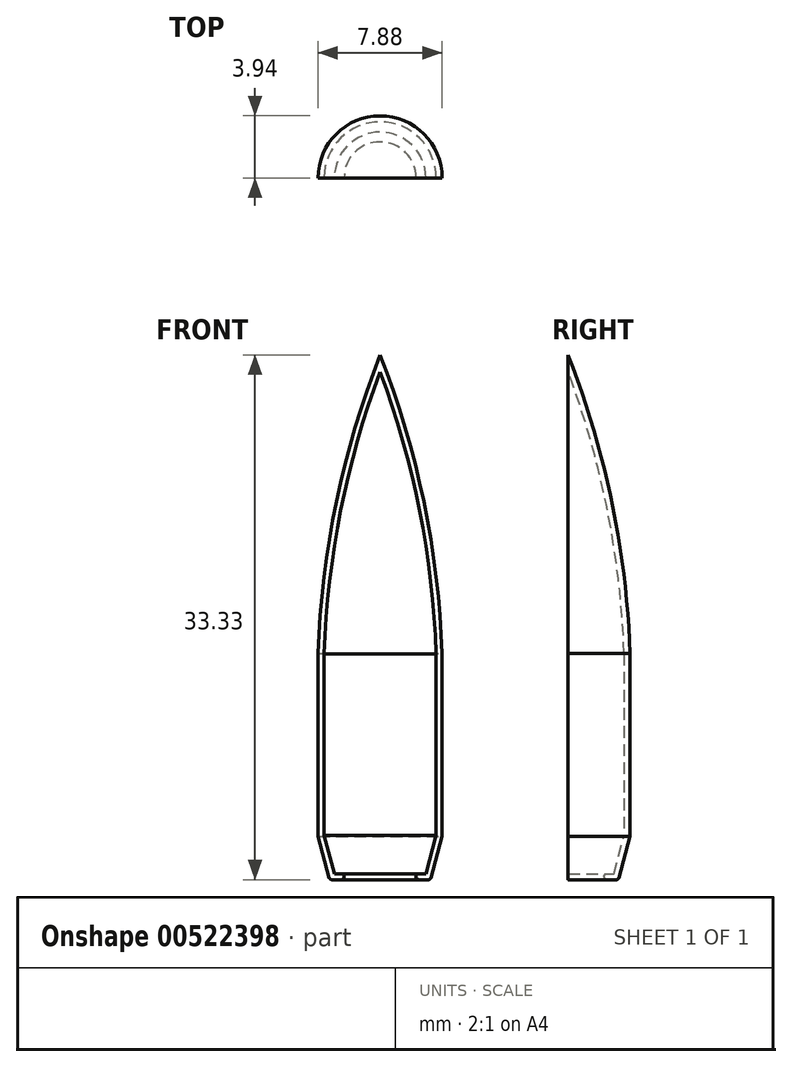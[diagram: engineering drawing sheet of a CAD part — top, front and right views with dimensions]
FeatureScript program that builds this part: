
annotation { "Feature Type Name" : "Feature", "Feature Type Description" : "" }
export const myFeature = defineFeature(function(context is Context, id is Id, definition is map)
    precondition{}
    {
        {
            var Q0;
            Q0=qCreatedBy(makeId("Front.planeOp"),FACE);
            var sketch = newSketch(context, id + "F0", { "sketchPlane" : qUnion([Q0])});
            skLineSegment(sketch, "E0", {"start": v(3.56, 2.43) * mm, "end": v(2.9, 0) * mm});
            skLineSegment(sketch, "E1", {"start": v(2.9, 0) * mm, "end": v(2.29, 0) * mm});
            skArc(sketch, "E2.trimOffspring", {"start": v(0, 31.88) * mm, "mid": v(2.5, 23.07) * mm, "end": v(3.56, 13.97) * mm});
            skLineSegment(sketch, "E3", {"start": v(-53.3, 11.99) * mm, "end": v(3.56, 13.97) * mm, "construction": true});
            skLineSegment(sketch, "E4", {"start": v(3.56, 2.43) * mm, "end": v(3.56, 13.97) * mm});
            skLineSegment(sketch, "E5.0", {"start": v(3.2, -0.38) * mm, "end": v(2.29, -0.38) * mm});
            skLineSegment(sketch, "E5.1", {"start": v(3.94, 2.38) * mm, "end": v(3.2, -0.38) * mm});
            skLineSegment(sketch, "E5.2", {"start": v(3.94, 2.38) * mm, "end": v(3.94, 13.98) * mm});
            skArc(sketch, "E5.3", {"start": v(0, 32.95) * mm, "mid": v(2.78, 23.63) * mm, "end": v(3.94, 13.98) * mm});
            skLineSegment(sketch, "E6", {"start": v(2.29, 0) * mm, "end": v(2.29, -0.38) * mm});
            skLineSegment(sketch, "E7.trimOffspring", {"start": v(0, 31.88) * mm, "end": v(0, 32.95) * mm});
            skSolve(sketch);
        }
        {
            var Q0;
            Q0 = qSketchRegion(id + "F0", true);
            var Q1;
            Q1=sQuery(id+"F0.wireOp",EDGE,"E7.trimOffspring");
            revolve(context, id + "F1", {"entities" : qUnion([Q0]), "axis" : qUnion([Q1]), "revolveType" : RevolveType.ONE_DIRECTION, "angle" : 180 * degree});
        }
        {
            var Q0;
            Q0=makeQuery(id+"F1.opRevolve","SWEPT_EDGE",EDGE,{"disambiguationData":[OSD([sQuery(id+"F0.wireOp",EDGE,"E1"),sQuery(id+"F0.wireOp",EDGE,"E6")])]});
            var Q1;
            Q1=makeQuery(id+"F1.opRevolve","SWEPT_EDGE",EDGE,{"disambiguationData":[OSD([sQuery(id+"F0.wireOp",EDGE,"E5.0"),sQuery(id+"F0.wireOp",EDGE,"E6")])]});
            var Q2;
            Q2=makeQuery(id+"F1.opRevolve","SWEPT_EDGE",EDGE,{"disambiguationData":[OSD([sQuery(id+"F0.wireOp",EDGE,"E5.0"),sQuery(id+"F0.wireOp",EDGE,"E5.1")])]});
            fillet(context, id + "F2", {"entities" : qUnion([Q0, Q1, Q2]), "tangentPropagation" : true, "radius" : 0.18 * mm, "defaultsChanged" : false, "vertexSettings" : [], "allowEdgeOverflow" : false});
        }
    });
